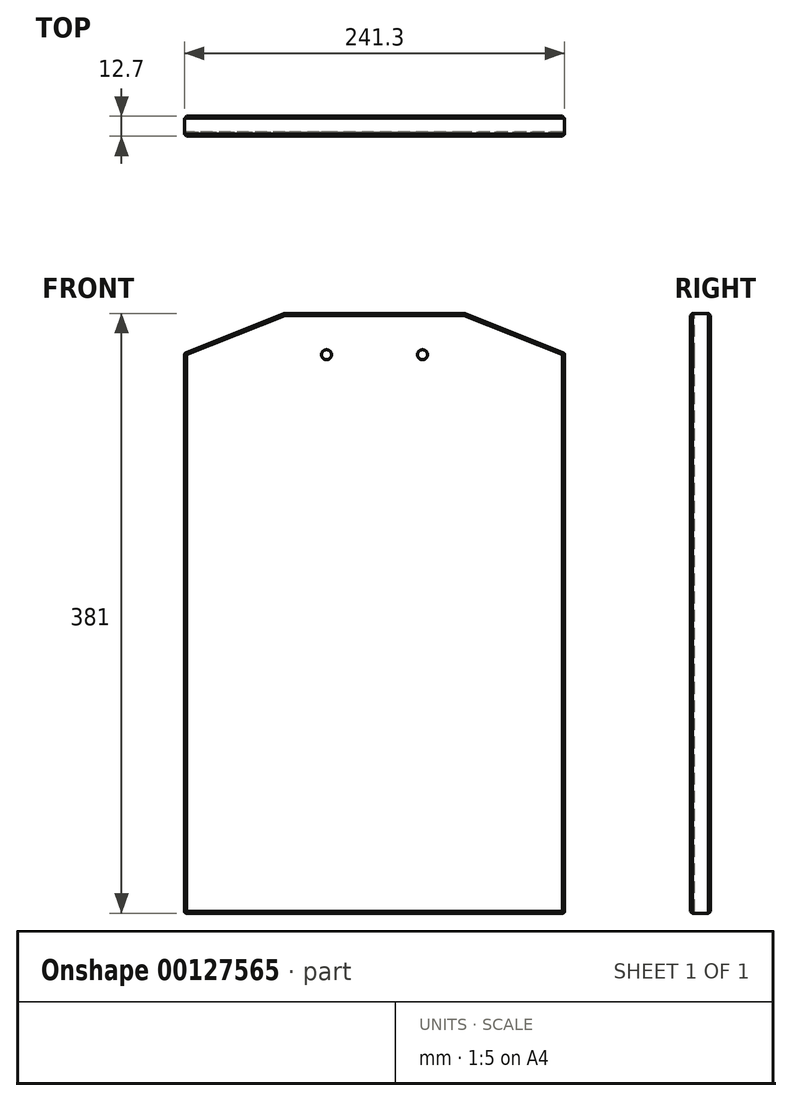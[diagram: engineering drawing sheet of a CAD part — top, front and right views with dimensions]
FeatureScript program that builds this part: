
annotation { "Feature Type Name" : "Feature", "Feature Type Description" : "" }
export const myFeature = defineFeature(function(context is Context, id is Id, definition is map)
    precondition{}
    {
        {
            var Q0;
            Q0=qCreatedBy(makeId("Front.planeOp"),FACE);
            var sketch = newSketch(context, id + "F0", { "sketchPlane" : qUnion([Q0])});
            skLineSegment(sketch, "E0.bottom", {"start": v(120.65, -190.5) * mm, "end": v(-120.65, -190.5) * mm});
            skLineSegment(sketch, "E0.top", {"start": v(120.65, 190.5) * mm, "end": v(-120.65, 190.5) * mm});
            skLineSegment(sketch, "E0.left", {"start": v(120.65, -190.5) * mm, "end": v(120.65, 190.5) * mm});
            skLineSegment(sketch, "E0.right", {"start": v(-120.65, -190.5) * mm, "end": v(-120.65, 190.5) * mm});
            skPoint(sketch, "E0.middle", {"position": v(0, 0) * mm});
            skLineSegment(sketch, "E1", {"start": v(-120.65, 165.1) * mm, "end": v(-57.15, 190.5) * mm});
            skLineSegment(sketch, "E2.MirrorCS", {"start": v(120.65, 165.1) * mm, "end": v(57.15, 190.5) * mm});
            skSolve(sketch);
        }
        {
            var Q0;
            {var subQ1=sQuery(id+"F0.wireOp",EDGE,"E0.bottom");Q0=makeQuery(id+"F0.imprint","IMPRINT",FACE,{"disambiguationData":[TD([[makeQuery(id+"F0.imprint","IMPRINT",EDGE,{"derivedFrom":subQ1}),-1.0]])]});}
            extrude(context, id + "F1", {"entities" : qUnion([Q0]), "depth" : 12.7 * mm});
        }
        {
            var Q0;
            Q0=makeQuery(id+"F1.opExtrude","CAP_EDGE",EDGE,{"disambiguationData":[OSD([sQuery(id+"F0.wireOp",EDGE,"E1")])],"isStart":false});
            var Q1;
            Q1=makeQuery(id+"F1.opExtrude","CAP_EDGE",EDGE,{"disambiguationData":[OSD([sQuery(id+"F0.wireOp",EDGE,"E0.top")])],"isStart":false});
            var Q2;
            Q2=makeQuery(id+"F1.opExtrude","CAP_EDGE",EDGE,{"disambiguationData":[OSD([sQuery(id+"F0.wireOp",EDGE,"E2.MirrorCS")])],"isStart":false});
            var Q3;
            Q3=makeQuery(id+"F1.opExtrude","CAP_EDGE",EDGE,{"disambiguationData":[OSD([sQuery(id+"F0.wireOp",EDGE,"E0.left")])],"isStart":false});
            var Q4;
            Q4=makeQuery(id+"F1.opExtrude","CAP_EDGE",EDGE,{"disambiguationData":[OSD([sQuery(id+"F0.wireOp",EDGE,"E0.bottom")])],"isStart":false});
            var Q5;
            Q5=makeQuery(id+"F1.opExtrude","CAP_EDGE",EDGE,{"disambiguationData":[OSD([sQuery(id+"F0.wireOp",EDGE,"E0.right")])],"isStart":false});
            var Q6;
            Q6=makeQuery(id+"F1.opExtrude","CAP_EDGE",EDGE,{"disambiguationData":[OSD([sQuery(id+"F0.wireOp",EDGE,"E0.left")])],"isStart":true});
            var Q7;
            Q7=makeQuery(id+"F1.opExtrude","CAP_EDGE",EDGE,{"disambiguationData":[OSD([sQuery(id+"F0.wireOp",EDGE,"E0.bottom")])],"isStart":true});
            var Q8;
            Q8=makeQuery(id+"F1.opExtrude","CAP_EDGE",EDGE,{"disambiguationData":[OSD([sQuery(id+"F0.wireOp",EDGE,"E0.right")])],"isStart":true});
            var Q9;
            Q9=makeQuery(id+"F1.opExtrude","CAP_EDGE",EDGE,{"disambiguationData":[OSD([sQuery(id+"F0.wireOp",EDGE,"E1")])],"isStart":true});
            var Q10;
            Q10=makeQuery(id+"F1.opExtrude","CAP_EDGE",EDGE,{"disambiguationData":[OSD([sQuery(id+"F0.wireOp",EDGE,"E0.top")])],"isStart":true});
            var Q11;
            Q11=makeQuery(id+"F1.opExtrude","CAP_EDGE",EDGE,{"disambiguationData":[OSD([sQuery(id+"F0.wireOp",EDGE,"E2.MirrorCS")])],"isStart":true});
            chamfer(context, id + "F2", {"entities" : qUnion([Q0, Q1, Q2, Q3, Q4, Q5, Q6, Q7, Q8, Q9, Q10, Q11]), "width" : 1.27 * mm, "tangentPropagation" : true});
        }
        {
            var Q0;
            Q0=makeQuery(id+"F1.opExtrude","SWEPT_EDGE",EDGE,{"disambiguationData":[OSD([sQuery(id+"F0.wireOp",EDGE,"E0.right"),sQuery(id+"F0.wireOp",EDGE,"E1")])]});
            var Q1;
            Q1=makeQuery(id+"F1.opExtrude","SWEPT_EDGE",EDGE,{"disambiguationData":[OSD([sQuery(id+"F0.wireOp",EDGE,"E0.top"),sQuery(id+"F0.wireOp",EDGE,"E1")])]});
            var Q2;
            Q2=makeQuery(id+"F1.opExtrude","SWEPT_EDGE",EDGE,{"disambiguationData":[OSD([sQuery(id+"F0.wireOp",EDGE,"E0.top"),sQuery(id+"F0.wireOp",EDGE,"E2.MirrorCS")])]});
            var Q3;
            Q3=makeQuery(id+"F1.opExtrude","SWEPT_EDGE",EDGE,{"disambiguationData":[OSD([sQuery(id+"F0.wireOp",EDGE,"E0.left"),sQuery(id+"F0.wireOp",EDGE,"E2.MirrorCS")])]});
            var Q4;
            Q4=makeQuery(id+"F1.opExtrude","SWEPT_EDGE",EDGE,{"disambiguationData":[OSD([sQuery(id+"F0.wireOp",EDGE,"E0.bottom"),sQuery(id+"F0.wireOp",EDGE,"E0.left")])]});
            var Q5;
            Q5=makeQuery(id+"F1.opExtrude","SWEPT_EDGE",EDGE,{"disambiguationData":[OSD([sQuery(id+"F0.wireOp",EDGE,"E0.bottom"),sQuery(id+"F0.wireOp",EDGE,"E0.right")])]});
            fillet(context, id + "F3", {"entities" : qUnion([Q0, Q1, Q2, Q3, Q4, Q5]), "radius" : 1.27 * mm, "tangentPropagation" : true, "allowEdgeOverflow" : false});
        }
        {
            var Q0;
            Q0=makeQuery(id+"F1.opExtrude","CAP_FACE",FACE,{"disambiguationData":[OSD([sQuery(id+"F0.wireOp",EDGE,"E0.bottom"),sQuery(id+"F0.wireOp",EDGE,"E0.top"),sQuery(id+"F0.wireOp",EDGE,"E0.left"),sQuery(id+"F0.wireOp",EDGE,"E0.right"),sQuery(id+"F0.wireOp",EDGE,"E1"),sQuery(id+"F0.wireOp",EDGE,"E2.MirrorCS")])],"isStart":false});
            var sketch = newSketch(context, id + "F4", { "sketchPlane" : qUnion([Q0])});
            skLineSegment(sketch, "E3", {"start": v(-119.38, 164.24) * mm, "end": v(119.38, 164.24) * mm});
            skCircle(sketch, "E4", {"center": v(-30.48, 164.24) * mm, "radius": 3.18 * mm});
            skCircle(sketch, "E5", {"center": v(30.48, 164.24) * mm, "radius": 3.18 * mm});
            skSolve(sketch);
        }
        {
            var Q0;
            {var subQ0=sQuery(id+"F4.wireOp",EDGE,"E5");var subQ1=sQuery(id+"F4.wireOp",EDGE,"E3");var subQ2=makeQuery(id+"F4.imprint","INTERSECT",VERTEX,{"disambiguationData":[OD(0.0)],"derivedFrom":[subQ1,subQ0]});Q0=makeQuery(id+"F4.imprint","IMPRINT",FACE,{"disambiguationData":[TD([[makeQuery(id+"F4.imprint","IMPRINT",EDGE,{"disambiguationData":[TD([[subQ2,-1.0]])],"derivedFrom":subQ1}),-1.0]])]});}
            var Q1;
            {var subQ0=sQuery(id+"F4.wireOp",EDGE,"E5");var subQ1=sQuery(id+"F4.wireOp",EDGE,"E3");var subQ2=makeQuery(id+"F4.imprint","INTERSECT",VERTEX,{"disambiguationData":[OD(0.0)],"derivedFrom":[subQ1,subQ0]});Q1=makeQuery(id+"F4.imprint","IMPRINT",FACE,{"disambiguationData":[TD([[makeQuery(id+"F4.imprint","IMPRINT",EDGE,{"disambiguationData":[TD([[subQ2,-1.0]])],"derivedFrom":subQ1}),1.0]])]});}
            var Q2;
            {var subQ0=sQuery(id+"F4.wireOp",EDGE,"E4");var subQ1=sQuery(id+"F4.wireOp",EDGE,"E3");var subQ2=makeQuery(id+"F4.imprint","INTERSECT",VERTEX,{"disambiguationData":[OD(0.0)],"derivedFrom":[subQ1,subQ0]});Q2=makeQuery(id+"F4.imprint","IMPRINT",FACE,{"disambiguationData":[TD([[makeQuery(id+"F4.imprint","IMPRINT",EDGE,{"disambiguationData":[TD([[subQ2,-1.0]])],"derivedFrom":subQ1}),1.0]])]});}
            var Q3;
            {var subQ0=sQuery(id+"F4.wireOp",EDGE,"E4");var subQ1=sQuery(id+"F4.wireOp",EDGE,"E3");var subQ2=makeQuery(id+"F4.imprint","INTERSECT",VERTEX,{"disambiguationData":[OD(0.0)],"derivedFrom":[subQ1,subQ0]});Q3=makeQuery(id+"F4.imprint","IMPRINT",FACE,{"disambiguationData":[TD([[makeQuery(id+"F4.imprint","IMPRINT",EDGE,{"disambiguationData":[TD([[subQ2,-1.0]])],"derivedFrom":subQ1}),-1.0]])]});}
            extrude(context, id + "F5", {"entities" : qUnion([Q0, Q1, Q2, Q3]), "operationType" : NewBodyOperationType.REMOVE, "oppositeDirection" : true, "depth" : 2.54 * mm});
        }
    });
